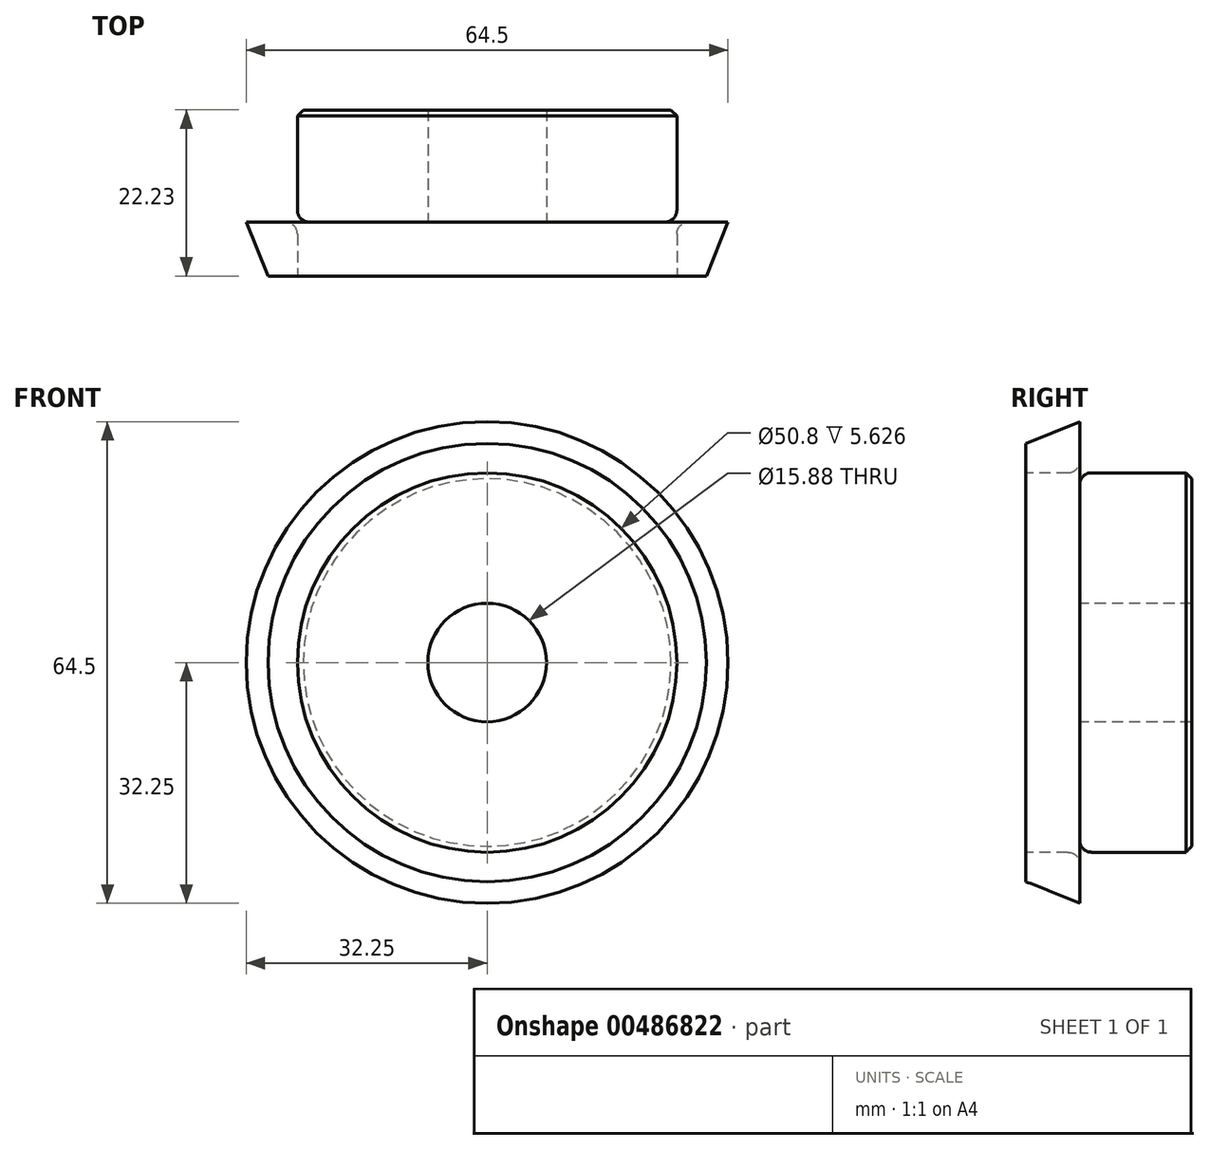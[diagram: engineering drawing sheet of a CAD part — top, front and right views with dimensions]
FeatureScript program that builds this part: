
annotation { "Feature Type Name" : "Feature", "Feature Type Description" : "" }
export const myFeature = defineFeature(function(context is Context, id is Id, definition is map)
    precondition{}
    {
        {
            var Q0;
            Q0=qCreatedBy(makeId("Right.planeOp"),FACE);
            var sketch = newSketch(context, id + "F0", { "sketchPlane" : qUnion([Q0])});
            skLineSegment(sketch, "E0", {"start": v(0, 0) * mm, "end": v(50.8, 0) * mm, "construction": true});
            skLineSegment(sketch, "E1.bottom", {"start": v(0, 7.94) * mm, "end": v(7.21, 7.94) * mm});
            skLineSegment(sketch, "E1.top", {"start": v(0, 35.69) * mm, "end": v(7.21, 35.69) * mm});
            skLineSegment(sketch, "E1.left", {"start": v(0, 7.94) * mm, "end": v(0, 35.69) * mm});
            skLineSegment(sketch, "E1.right", {"start": v(7.21, 7.94) * mm, "end": v(7.21, 35.69) * mm});
            skLineSegment(sketch, "E2.bottom", {"start": v(0, 7.94) * mm, "end": v(22.23, 7.94) * mm});
            skLineSegment(sketch, "E2.top", {"start": v(0, 25.4) * mm, "end": v(22.23, 25.4) * mm});
            skLineSegment(sketch, "E2.left", {"start": v(0, 7.94) * mm, "end": v(0, 25.4) * mm});
            skLineSegment(sketch, "E2.right", {"start": v(22.23, 7.94) * mm, "end": v(22.23, 25.4) * mm});
            skLineSegment(sketch, "E3.MirrorCS", {"start": v(0, -7.94) * mm, "end": v(7.21, -7.94) * mm});
            skLineSegment(sketch, "E4.MirrorCS", {"start": v(22.23, -7.94) * mm, "end": v(22.23, -25.4) * mm});
            skLineSegment(sketch, "E5.MirrorCS", {"start": v(0, -7.94) * mm, "end": v(0, -25.4) * mm});
            skLineSegment(sketch, "E6.MirrorCS", {"start": v(0, -35.69) * mm, "end": v(7.21, -35.69) * mm});
            skLineSegment(sketch, "E7.MirrorCS", {"start": v(0, -7.94) * mm, "end": v(0, -35.69) * mm});
            skLineSegment(sketch, "E8.MirrorCS", {"start": v(7.21, -7.94) * mm, "end": v(7.21, -35.69) * mm});
            skLineSegment(sketch, "E9.MirrorCS", {"start": v(0, -7.94) * mm, "end": v(22.23, -7.94) * mm});
            skLineSegment(sketch, "E10.MirrorCS", {"start": v(0, -25.4) * mm, "end": v(22.23, -25.4) * mm});
            skSolve(sketch);
        }
        {
            var Q0;
            {var subQ5=sQuery(id+"F0.wireOp",EDGE,"E2.right");Q0=makeQuery(id+"F0.imprint","IMPRINT",FACE,{"disambiguationData":[TD([[makeQuery(id+"F0.imprint","IMPRINT",EDGE,{"derivedFrom":subQ5}),1.0]])]});}
            var Q1;
            {var subQ5=sQuery(id+"F0.wireOp",EDGE,"E2.left");Q1=makeQuery(id+"F0.imprint","IMPRINT",FACE,{"disambiguationData":[TD([[makeQuery(id+"F0.imprint","IMPRINT",EDGE,{"derivedFrom":subQ5}),-1.0]])]});}
            var Q2;
            {var subQ0=sQuery(id+"F0.wireOp",EDGE,"E1.top");Q2=makeQuery(id+"F0.imprint","IMPRINT",FACE,{"disambiguationData":[TD([[makeQuery(id+"F0.imprint","IMPRINT",EDGE,{"derivedFrom":subQ0}),-1.0]])]});}
            var Q3;
            Q3=sQuery(id+"F0.wireOp",EDGE,"E0");
            revolve(context, id + "F1", {"entities" : qUnion([Q0, Q1, Q2]), "axis" : qUnion([Q3]), "revolveType" : RevolveType.FULL});
        }
        {
            var Q0;
            Q0=makeQuery(id+"F1.opRevolve","SWEPT_EDGE",EDGE,{"disambiguationData":[OSD([sQuery(id+"F0.wireOp",EDGE,"E1.right"),sQuery(id+"F0.wireOp",EDGE,"E2.top")])]});
            fillet(context, id + "F2", {"entities" : qUnion([Q0]), "radius" : 1.59 * mm, "tangentPropagation" : true, "allowEdgeOverflow" : false});
        }
        {
            var Q0;
            Q0=makeQuery(id+"F1.opRevolve","SWEPT_EDGE",EDGE,{"disambiguationData":[OSD([sQuery(id+"F0.wireOp",EDGE,"E2.top"),sQuery(id+"F0.wireOp",EDGE,"E2.right")])]});
            chamfer(context, id + "F3", {"entities" : qUnion([Q0]), "width" : 0.8 * mm, "tangentPropagation" : true});
        }
        {
            var Q0;
            Q0=makeQuery(id+"F1.opRevolve","SWEPT_EDGE",EDGE,{"disambiguationData":[OSD([sQuery(id+"F0.wireOp",EDGE,"E1.top"),sQuery(id+"F0.wireOp",EDGE,"E1.left")])]});
            chamfer(context, id + "F4", {"entities" : qUnion([Q0]), "chamferType" : ChamferType.TWO_OFFSETS, "width1" : 6.35 * mm, "oppositeDirection" : false, "width2" : 15.75 * mm, "tangentPropagation" : true});
        }
    });
